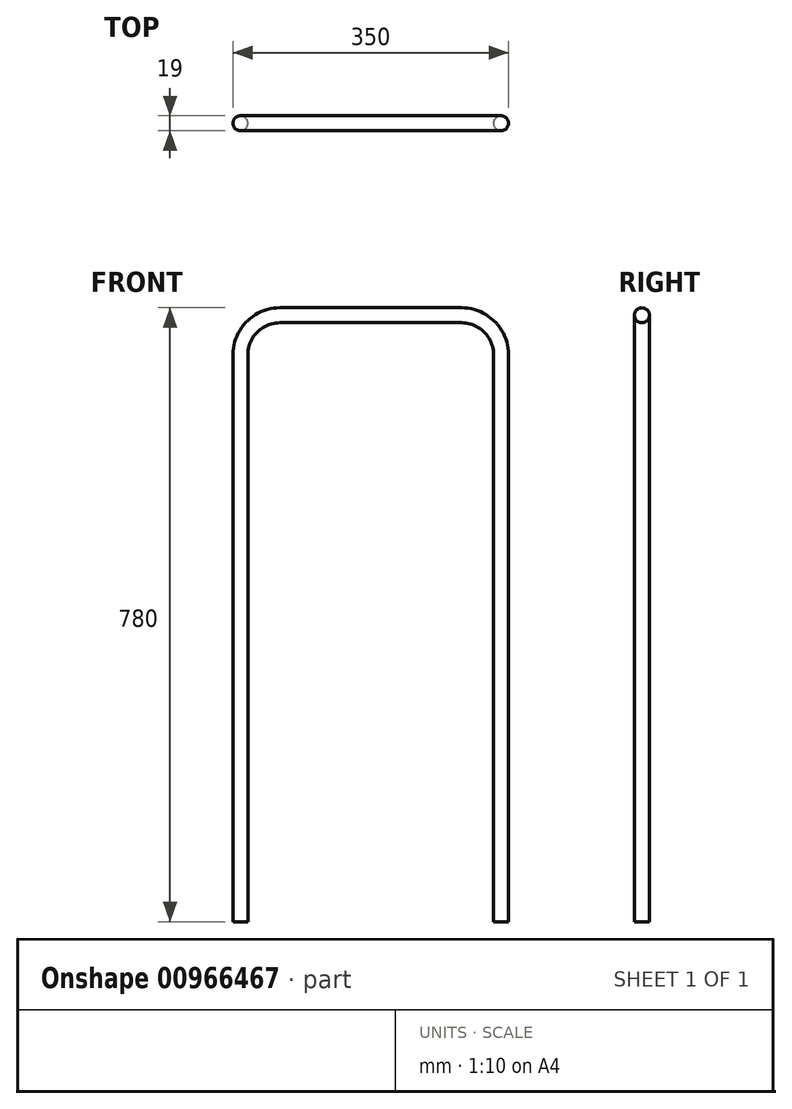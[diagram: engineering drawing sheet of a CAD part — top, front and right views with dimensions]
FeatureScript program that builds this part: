
annotation { "Feature Type Name" : "Feature", "Feature Type Description" : "" }
export const myFeature = defineFeature(function(context is Context, id is Id, definition is map)
    precondition{}
    {
        {
            var Q0;
            Q0=qCreatedBy(makeId("Front.planeOp"),FACE);
            var sketch = newSketch(context, id + "F0", { "sketchPlane" : qUnion([Q0])});
            skLineSegment(sketch, "E0", {"start": v(-60.7, 0) * mm, "end": v(-60.7, 720.5) * mm});
            skLineSegment(sketch, "E1", {"start": v(-10.7, 770.5) * mm, "end": v(220.3, 770.5) * mm});
            skLineSegment(sketch, "E2", {"start": v(270.3, 720.5) * mm, "end": v(270.3, 0) * mm});
            skPoint(sketch, "E3.visualSharp", {"position": v(-60.7, 770.5) * mm});
            skArc(sketch, "E3.filletArc", {"start": v(-10.7, 770.5) * mm, "mid": v(-46.05, 755.86) * mm, "end": v(-60.7, 720.5) * mm});
            skPoint(sketch, "E4.visualSharp", {"position": v(270.3, 770.5) * mm});
            skArc(sketch, "E4.filletArc", {"start": v(270.3, 720.5) * mm, "mid": v(255.66, 755.86) * mm, "end": v(220.3, 770.5) * mm});
            skSolve(sketch);
        }
        {
            var Q0;
            Q0=sQuery(id+"F0.wireOp",EDGE,"E0");
            var Q1;
            Q1=sQuery(id+"F0.wireOp",VERTEX,"E0.start");
            var Q2;
            Q2 = qBodyType(qCreatedBy(id + "F2" ,EDGE), BodyType.WIRE);
            cPlane(context, id + "F1", {"entities" : qUnion([Q0, Q1, Q2]), "cplaneType" : CPlaneType.CURVE_POINT, "offset" : 0 * mm, "width" : 150 * mm, "height" : 150 * mm});
        }
        {
            var Q0;
            Q0=qCreatedBy(id+"F1.planeOp",FACE);
            var sketch = newSketch(context, id + "F2", { "sketchPlane" : qUnion([Q0])});
            skCircle(sketch, "E5", {"center": v(-60.7, 0) * mm, "radius": 9.5 * mm});
            skSolve(sketch);
        }
        {
            var Q0;
            Q0=makeQuery(id+"F2.imprint","IMPRINT",FACE,{"disambiguationData":[TD([[makeQuery(id+"F2.imprint","IMPRINT",EDGE,{"derivedFrom":sQuery(id+"F2.wireOp",EDGE,"E5")}),1.0]])]});
            var Q1;
            Q1=sQuery(id+"F0.wireOp",EDGE,"E0");
            var Q2;
            Q2=sQuery(id+"F0.wireOp",EDGE,"E3.filletArc");
            var Q3;
            Q3=sQuery(id+"F0.wireOp",EDGE,"E1");
            var Q4;
            Q4=sQuery(id+"F0.wireOp",EDGE,"E4.filletArc");
            var Q5;
            Q5=sQuery(id+"F0.wireOp",EDGE,"E2");
            sweep(context, id + "F3", {"profiles" : qUnion([Q0]), "path" : qUnion([Q1, Q2, Q3, Q4, Q5])});
        }
    });
